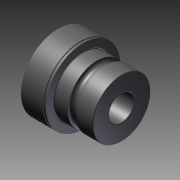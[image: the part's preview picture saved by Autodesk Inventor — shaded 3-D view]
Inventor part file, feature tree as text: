
AUTODESK INVENTOR PART (.ipt)
format: ipt  version: 2011 SP1 (Build 150282100, 282)  size: 218,624 bytes
history: native  units: mm
features: other x7, revolve x1, sketch x1
ambient origin geometry x8: Origin, YZ Plane, XZ Plane, XY Plane, X Axis, Y Axis, Z Axis, Center Point
bodies: Solid1 (feature_tree)
feature tree (9):
  revolve  "Revolution1"  [1 undecoded]
  other  "to_housing_XY"
  other  "to_housing_YZ"
  other  "to_housing_ZX"
  other  "to_housing_X"
  other  "to_housing_Y"
  other  "to_housing_Z"
  other  "to_housing_Center"
  sketch  "Sketch_1"  dims[d0=360.0deg d1=0.0mm]
note: 1 required parameter value undecoded (feature->parameter linkage not recoverable at this tier; creation-order binding heuristic only, values carry confidence <= 0.55)
